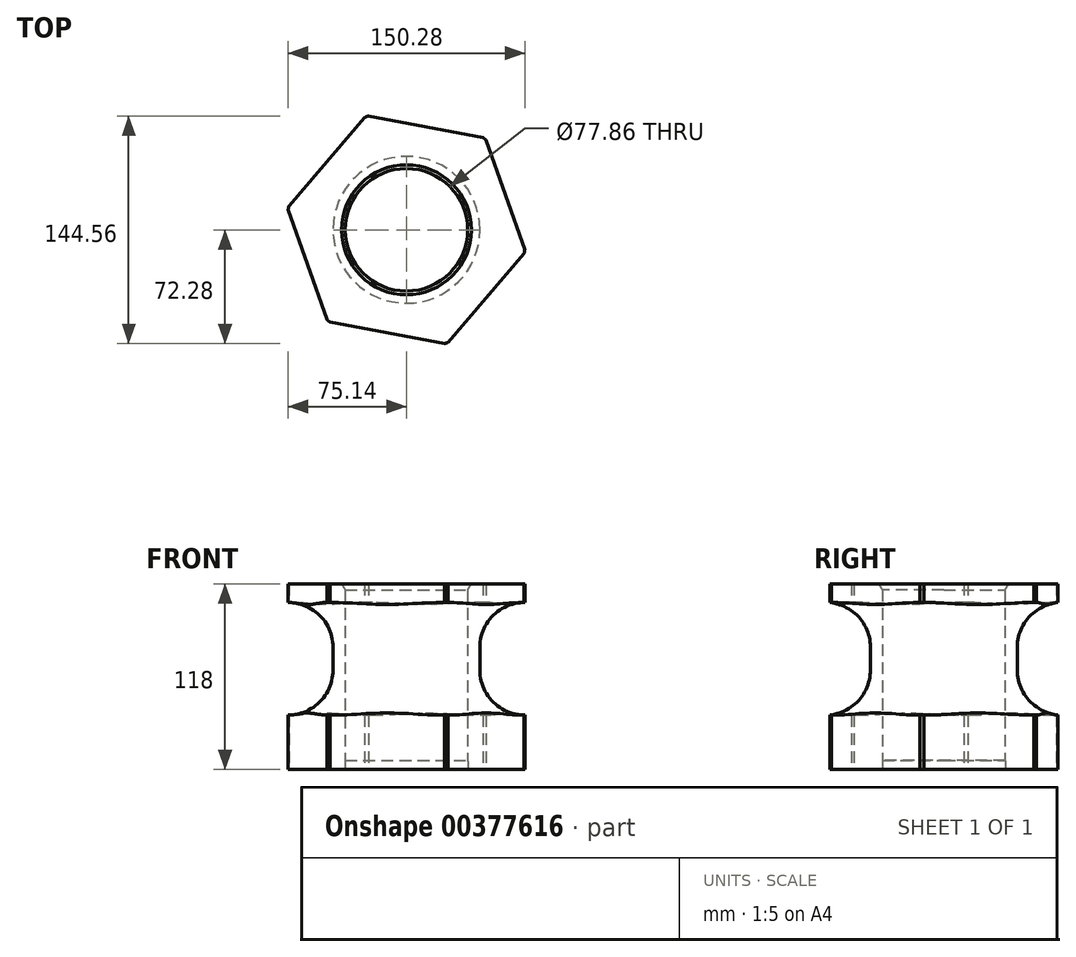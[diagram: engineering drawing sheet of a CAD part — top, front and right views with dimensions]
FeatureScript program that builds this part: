
annotation { "Feature Type Name" : "Feature", "Feature Type Description" : "" }
export const myFeature = defineFeature(function(context is Context, id is Id, definition is map)
    precondition{}
    {
        {
            var Q0;
            Q0=qCreatedBy(makeId("Front.planeOp"),FACE);
            var sketch = newSketch(context, id + "F0", { "sketchPlane" : qUnion([Q0])});
            skLineSegment(sketch, "E0", {"start": v(76.22, 0) * mm, "end": v(76.22, 34.55) * mm});
            skLineSegment(sketch, "E1", {"start": v(78.95, 155.24) * mm, "end": v(46.42, 155.24) * mm});
            skLineSegment(sketch, "E2", {"start": v(11.54, 92.63) * mm, "end": v(11.54, 54.77) * mm});
            skLineSegment(sketch, "E3", {"start": v(38.93, 0) * mm, "end": v(76.22, 0) * mm});
            skPoint(sketch, "E4", {"position": v(-32.97, 184.76) * mm});
            skPoint(sketch, "E5", {"position": v(23.73, 252.28) * mm});
            skArc(sketch, "E6", {"start": v(11.54, 92.63) * mm, "mid": v(40.88, 117.31) * mm, "end": v(46.42, 155.24) * mm});
            skArc(sketch, "E7", {"start": v(38.93, 0) * mm, "mid": v(32.36, 30.94) * mm, "end": v(11.54, 54.77) * mm});
            skLineSegment(sketch, "E8", {"start": v(78.95, 155.24) * mm, "end": v(78.95, 105.76) * mm});
            skLineSegment(sketch, "E9", {"start": v(46.63, 77.67) * mm, "end": v(46.63, 63.2) * mm});
            skArc(sketch, "E10", {"start": v(78.95, 105.76) * mm, "mid": v(56.39, 99.08) * mm, "end": v(46.63, 77.67) * mm});
            skArc(sketch, "E11", {"start": v(46.63, 63.2) * mm, "mid": v(55.35, 42.61) * mm, "end": v(76.22, 34.55) * mm});
            skSolve(sketch);
        }
        {
            var Q0;
            Q0=makeQuery(id+"F0.imprint","IMPRINT",FACE,{"disambiguationData":[TD([[makeQuery(id+"F0.imprint","IMPRINT",EDGE,{"derivedFrom":sQuery(id+"F0.wireOp",EDGE,"E0")}),1.0]])]});
            var sketch = newSketch(context, id + "F1", { "sketchPlane" : qUnion([Q0])});
            skLineSegment(sketch, "E12", {"start": v(0, 132.86) * mm, "end": v(0, 0) * mm});
            skSolve(sketch);
        }
        {
            var Q0;
            Q0=makeQuery(id+"F0.imprint","IMPRINT",FACE,{"disambiguationData":[TD([[makeQuery(id+"F0.imprint","IMPRINT",EDGE,{"derivedFrom":sQuery(id+"F0.wireOp",EDGE,"E0")}),1.0]])]});
            var Q1;
            Q1=sQuery(id+"F1.wireOp",EDGE,"E12");
            revolve(context, id + "F2", {"entities" : qUnion([Q0]), "axis" : qUnion([Q1]), "revolveType" : RevolveType.FULL});
        }
        {
            var Q0;
            Q0=makeQuery(id+"F2.opRevolve","SWEPT_EDGE",EDGE,{"disambiguationData":[OSD([sQuery(id+"F0.wireOp",EDGE,"E1"),sQuery(id+"F0.wireOp",EDGE,"0932af63-492e-4285-a4d0-6ece1db173c6")])]});
            var Q1;
            Q1=makeQuery(id+"F2.opRevolve","SWEPT_EDGE",EDGE,{"disambiguationData":[OSD([sQuery(id+"F0.wireOp",EDGE,"84de2e9d-350c-476c-89be-a605c5b4d564"),sQuery(id+"F0.wireOp",EDGE,"E1")])]});
            fillet(context, id + "F3", {"entities" : qUnion([Q0, Q1]), "radius" : 5 * mm, "tangentPropagation" : true, "allowEdgeOverflow" : false});
        }
        {
            var Q0;
            Q0=makeQuery(id+"F2.opRevolve","SWEPT_FACE",FACE,{"disambiguationData":[OSD([sQuery(id+"F0.wireOp",EDGE,"E3")])]});
            var sketch = newSketch(context, id + "F4", { "sketchPlane" : qUnion([Q0])});
            skCircle(sketch, "E13.cCircle", {"center": v(0, 0) * mm, "radius": 66.62 * mm, "construction": true});
            skLineSegment(sketch, "E13.0", {"start": v(-75.62, -14.12) * mm, "end": v(-50.04, 58.43) * mm});
            skLineSegment(sketch, "E13.1", {"start": v(-50.04, 58.43) * mm, "end": v(25.58, 72.55) * mm});
            skLineSegment(sketch, "E13.2", {"start": v(25.58, 72.55) * mm, "end": v(75.62, 14.12) * mm});
            skLineSegment(sketch, "E13.3", {"start": v(75.62, 14.12) * mm, "end": v(50.04, -58.43) * mm});
            skLineSegment(sketch, "E13.4", {"start": v(50.04, -58.43) * mm, "end": v(-25.58, -72.55) * mm});
            skLineSegment(sketch, "E13.5", {"start": v(-25.58, -72.55) * mm, "end": v(-75.62, -14.12) * mm});
            skPoint(sketch, "E13.0.midPoint", {"position": v(-62.83, 22.16) * mm});
            skSolve(sketch);
        }
        {
            var Q0;
            {var subQ1=sQuery(id+"F0.wireOp",EDGE,"E3");Q0=makeQuery(id+"F4.imprint","IMPRINT",FACE,{"disambiguationData":[TD([[makeQuery(id+"F4.imprint","IMPRINT",EDGE,{"derivedFrom":makeQuery(id+"F2.opRevolve","SWEPT_EDGE",EDGE,{"disambiguationData":[OSD([subQ1,sQuery(id+"F0.wireOp",EDGE,"E7")])]})}),1.0]])]});}
            extrude(context, id + "F5", {"entities" : qUnion([Q0]), "operationType" : NewBodyOperationType.INTERSECT, "depth" : -118 * mm});
        }
    });
